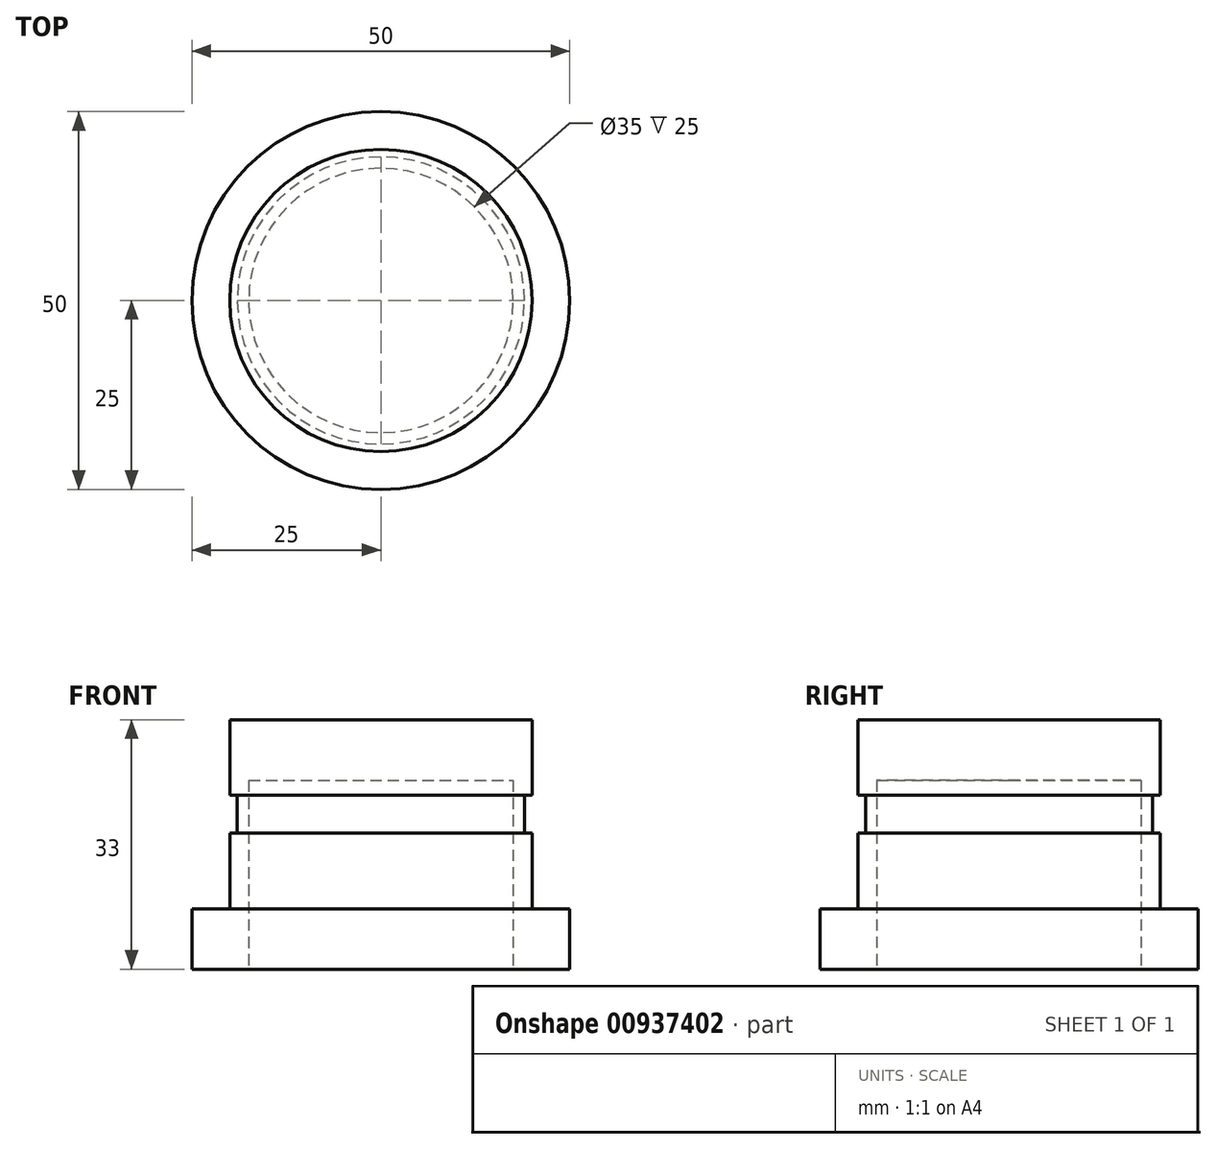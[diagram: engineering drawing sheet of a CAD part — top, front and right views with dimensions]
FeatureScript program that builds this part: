
annotation { "Feature Type Name" : "Feature", "Feature Type Description" : "" }
export const myFeature = defineFeature(function(context is Context, id is Id, definition is map)
    precondition{}
    {
        {
            var Q0;
            Q0=qCreatedBy(makeId("Top.planeOp"),FACE);
            var sketch = newSketch(context, id + "F0", { "sketchPlane" : qUnion([Q0])});
            skCircle(sketch, "E0", {"center": v(0, 0) * mm, "radius": 25 * mm});
            skSolve(sketch);
        }
        {
            var Q0;
            Q0 = qSketchRegion(id + "F0", true);
            extrude(context, id + "F1", {"entities" : qUnion([Q0]), "depth" : 8 * mm, "offsetDistance" : 25 * mm});
        }
        {
            var Q0;
            Q0=makeQuery(id+"F1.opExtrude","CAP_FACE",FACE,{"disambiguationData":[OSD([sQuery(id+"F0.wireOp",EDGE,"E0")])],"isStart":false});
            var sketch = newSketch(context, id + "F2", { "sketchPlane" : qUnion([Q0])});
            skCircle(sketch, "E1", {"center": v(0, 0) * mm, "radius": 20 * mm});
            skSolve(sketch);
        }
        {
            var Q0;
            Q0 = qSketchRegion(id + "F2", true);
            extrude(context, id + "F3", {"entities" : qUnion([Q0]), "operationType" : NewBodyOperationType.ADD, "depth" : 10 * mm, "offsetDistance" : 25 * mm});
        }
        {
            var Q0;
            Q0=makeQuery(id+"F3.opExtrude","CAP_FACE",FACE,{"disambiguationData":[OSD([sQuery(id+"F2.wireOp",EDGE,"E1")])],"isStart":false});
            var sketch = newSketch(context, id + "F4", { "sketchPlane" : qUnion([Q0])});
            skCircle(sketch, "E2", {"center": v(0, 0) * mm, "radius": 19 * mm});
            skSolve(sketch);
        }
        {
            var Q0;
            Q0 = qSketchRegion(id + "F4", true);
            extrude(context, id + "F5", {"entities" : qUnion([Q0]), "operationType" : NewBodyOperationType.ADD, "depth" : 5 * mm, "offsetDistance" : 25 * mm});
        }
        {
            var Q0;
            Q0=makeQuery(id+"F5.opExtrude","CAP_FACE",FACE,{"disambiguationData":[OSD([sQuery(id+"F4.wireOp",EDGE,"E2")])],"isStart":false});
            var sketch = newSketch(context, id + "F6", { "sketchPlane" : qUnion([Q0])});
            skCircle(sketch, "E3", {"center": v(0, 0) * mm, "radius": 20 * mm});
            skSolve(sketch);
        }
        {
            var Q0;
            Q0 = qSketchRegion(id + "F6", true);
            extrude(context, id + "F7", {"entities" : qUnion([Q0]), "operationType" : NewBodyOperationType.ADD, "depth" : 10 * mm, "offsetDistance" : 25 * mm});
        }
        {
            var Q0;
            Q0=makeQuery(id+"F1.opExtrude","CAP_FACE",FACE,{"disambiguationData":[OSD([sQuery(id+"F0.wireOp",EDGE,"E0")])],"isStart":true});
            var sketch = newSketch(context, id + "F8", { "sketchPlane" : qUnion([Q0])});
            skCircle(sketch, "E4", {"center": v(0, 0) * mm, "radius": 17.5 * mm});
            skSolve(sketch);
        }
        {
            var Q0;
            Q0 = qSketchRegion(id + "F8", true);
            extrude(context, id + "F9", {"entities" : qUnion([Q0]), "operationType" : NewBodyOperationType.REMOVE, "oppositeDirection" : true, "depth" : 25 * mm, "offsetDistance" : 25 * mm});
        }
    });
